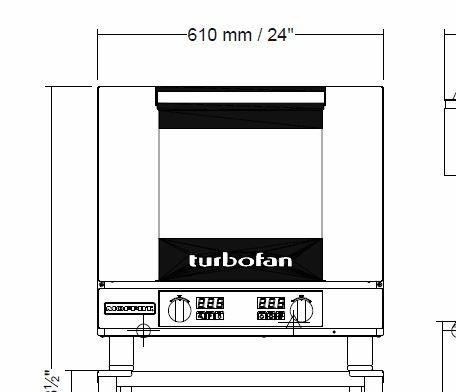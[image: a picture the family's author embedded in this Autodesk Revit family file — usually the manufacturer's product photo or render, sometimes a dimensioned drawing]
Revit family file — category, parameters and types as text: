
# Revit family: QF_MOFFAT_E30M3-2C_NZ
name_source: partatom
category: Specialty Equipment
revit_build: Autodesk Revit 2014 (Build: 20130308_1515(x64)
units: mm (PartAtom-declared; Revit-internal decimal feet)

## types (1)
- QF_MOFFAT_E30M3-2C_NZ
    Apparent Power = 2185 VA
    Conn Conduit = Yes
    Depth = 666 mm  [stored 2.18504 ft]
    Description = GN 1/1 MANUAL / ELECTRIC CONVECTION OVENS DOUBLE STACKED ON A STAINLESS STEEL BASE STAND
    Elec Conn Connection Height = 0 mm  [stored 0 ft]
    Elec Conn RI Height = 0 mm  [stored 0 ft]
    Electrical Remarks = 230-240V, 50Hz, 1P+N+E, 2.3kW, 9.5A
    Exhaust RI Height = 0 mm  [stored 0 ft]
    Exhaust Static Press = 0.00 in-wg
    Exhaust Vent Depth = 0 mm  [stored 0 ft]
    Exhaust Vent Diameter = 0 mm  [stored 0 ft]
    Exhaust Vent Width = 0 mm  [stored 0 ft]
    Exhaust Volume = 0 CFM
    FL Amps = 10 A
    Foodservice Equipment Identifier = Yes
    Height = 1718 mm  [stored 5.63648 ft]
    Height of Stand = 536 mm  [stored 1.75853 ft]
    Identify Quantity as Lot = Yes
    Length = 810 mm  [stored 2.65748 ft]
    Manufacturer = MOFFAT
    Max Overcurrent Protection = 0 A
    Min Ckt Ampacity = 0 A
    Model = E30M3-2C
    Number of Poles = 1
    Phase = 1
    Volts = 230 V
    Watts = 2300 W
    Weight in Pounds = 0

note: [stored X ft] marks values corroborated as IEEE doubles in the binary element streams (Revit-internal decimal feet)

## geometry (parser evidence)
native form markers: Blend x14, Sweep x7
no freeform markers — native parametric forms only
